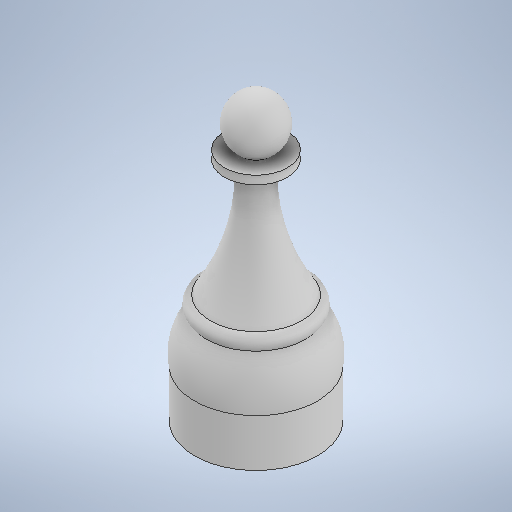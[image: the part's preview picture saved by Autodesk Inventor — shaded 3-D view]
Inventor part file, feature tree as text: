
AUTODESK INVENTOR PART (.ipt)
format: ipt  version: 2025.1 (Build 291241000, 241)  size: 312,320 bytes
history: native  units: mm
features: other x1, revolve x1, sketch x1
ambient origin geometry x8: Origin, YZ Plane, XZ Plane, XY Plane, X Axis, Y Axis, Z Axis, Center Point
bodies: Body1 (feature_tree)
feature tree (3):
  other  "Sólido1"
  revolve  "Revolución1"  Angle=90.0deg
  sketch  "Boceto1"  dims[d0=50.0mm d1=90.0deg]
